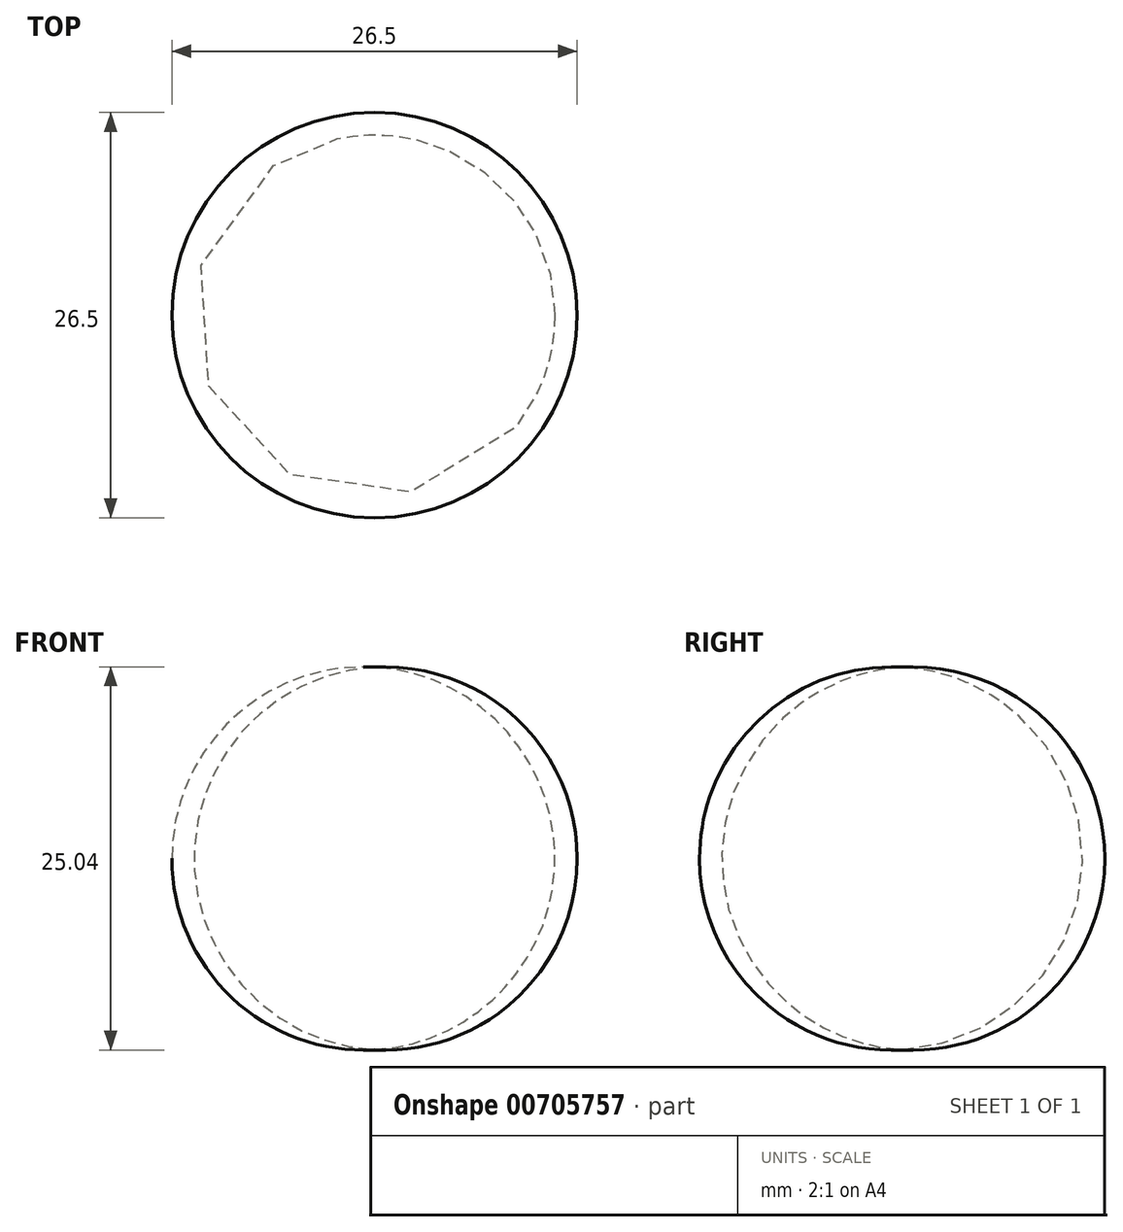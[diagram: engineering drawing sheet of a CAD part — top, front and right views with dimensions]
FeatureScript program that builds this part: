
annotation { "Feature Type Name" : "Feature", "Feature Type Description" : "" }
export const myFeature = defineFeature(function(context is Context, id is Id, definition is map)
    precondition{}
    {
        {
            var Q0;
            Q0=qCreatedBy(makeId("Front.planeOp"),FACE);
            var sketch = newSketch(context, id + "F0", { "sketchPlane" : qUnion([Q0])});
            skLineSegment(sketch, "E0", {"start": v(0, 0) * mm, "end": v(0, 25) * mm});
            skArc(sketch, "E1", {"start": v(0, 0) * mm, "mid": v(13.25, 12.5) * mm, "end": v(0, 25) * mm});
            skSolve(sketch);
        }
        {
            var Q0;
            Q0=makeQuery(id+"F0.imprint","IMPRINT",FACE,{"disambiguationData":[TD([[makeQuery(id+"F0.imprint","IMPRINT",EDGE,{"derivedFrom":sQuery(id+"F0.wireOp",EDGE,"E0")}),-1.0]])]});
            var Q1;
            Q1=sQuery(id+"F0.wireOp",EDGE,"E0");
            revolve(context, id + "F1", {"surfaceOperationType" : NewSurfaceOperationType.NEW, "entities" : qUnion([Q0]), "axis" : qUnion([Q1]), "revolveType" : RevolveType.FULL});
        }
    });
